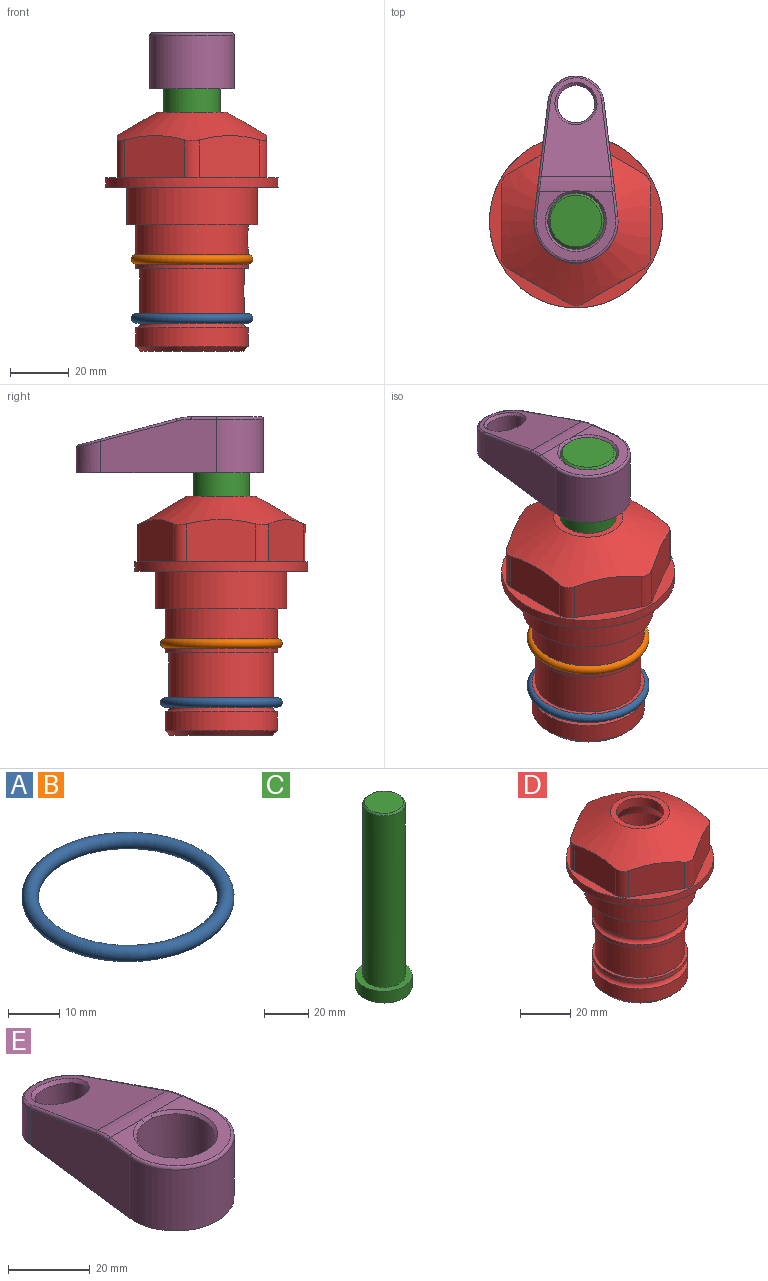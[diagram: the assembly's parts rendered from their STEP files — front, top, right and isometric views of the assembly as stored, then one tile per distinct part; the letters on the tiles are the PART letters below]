
ASSEMBLY  parts=5 mates=4
PART A: 1 faces, bbox 44.7x44.7x3.2 mm
  f0: torus R=19.05mm, axis (0,0,1), area 1193.9mm2
PART B: same geometry as A
PART C: 6 faces, bbox 25.4x25.4x101.6 mm
  f0: plane 17.46x17.46mm, normal (0,0,1), area 239.5mm2, adj f5
  f1: plane 25.4x25.4mm, normal (0,0,-1), area 506.7mm2, adj f2
  f2: cylinder r=12.7mm len=25.4mm, axis (0,0,1), area 506.7mm2, adj f1,f3
  f3: plane 25.4x25.4mm, normal (0,0,1), area 221.7mm2, adj f2,f4
  f4: cylinder r=9.53mm len=94.46mm, axis (0,0,1), area 5653mm2, adj f3,f5
  f5: cone r=8.73mm half-angle=45deg, axis (0,0,-1), area 64.4mm2, adj f0,f4
PART D: 36 faces, bbox 58.7x58.7x81 mm
  f0: cylinder r=17.78mm len=35.56mm, axis (0,0,1), area 1670.8mm2, adj f23,f24,f31
  f1: cylinder r=19.05mm len=38.1mm, axis (0,0,1), area 1191.9mm2, adj f26,f27,f30
  f2: plane 58.66x58.66mm, normal (0,0,-1), area 1150.6mm2, adj f3,f28
  f3: cylinder r=29.33mm len=58.66mm, axis (0,0,-1), area 585.1mm2, adj f2,f4
  f4: plane 58.66x58.66mm, normal (0,0,1), area 475.9mm2, adj f3,f5,f6,f7,f8,f9,f10,f11
  f5: plane 20.32x14.34mm, normal (-0.5,0.87,0), area 324.4mm2, adj f4,f15,f16,f17
  f6: plane 20.32x14.34mm, normal (0.5,0.87,0), area 324.4mm2, adj f4,f14,f15,f17
  f7: plane 23.48x14.34mm, normal (1,0,0), area 324.4mm2, adj f4,f13,f14,f17
  f8: plane 20.32x14.34mm, normal (0.5,-0.87,0), area 324.4mm2, adj f4,f12,f13,f17
  f9: plane 20.32x14.34mm, normal (-0.5,-0.87,0), area 324.4mm2, adj f4,f11,f12,f17
  f10: plane 23.48x14.34mm, normal (-1,0,0), area 324.4mm2, adj f4,f11,f16,f17
  f11: cylinder r=5.08mm len=12.85mm, axis (0,0,-1), area 67.2mm2, adj f4,f9,f10,f17
  f12: cylinder r=5.08mm len=12.85mm, axis (0,0,-1), area 67.2mm2, adj f4,f8,f9,f17
  f13: cylinder r=5.08mm len=12.85mm, axis (0,0,-1), area 67.2mm2, adj f4,f7,f8,f17
  f14: cylinder r=5.08mm len=12.85mm, axis (0,0,-1), area 67.2mm2, adj f4,f6,f7,f17
  f15: cylinder r=5.08mm len=12.85mm, axis (0,0,-1), area 67.2mm2, adj f4,f5,f6,f17
  f16: cylinder r=5.08mm len=12.85mm, axis (0,0,-1), area 67.2mm2, adj f4,f5,f10,f17
  f17: cone r=11.73mm half-angle=60deg, axis (0,0,-1), area 2071.8mm2, adj f5,f6,f7,f8,f9,f10,f11,f12
  f18: plane 23.46x23.46mm, normal (0,0,1), area 147.4mm2, adj f17,f35
  f19: plane 34.93x34.93mm, normal (0,0,-1), area 958mm2, adj f29
  f20: cylinder r=19.05mm len=38.1mm, axis (0,0,1), area 760.1mm2, adj f21,f29
  f21: torus R=19.05mm, axis (0,0,1), area 565.3mm2, adj f20,f22
  f22: cylinder r=19.05mm len=38.1mm, axis (0,0,1), area 190mm2, adj f21,f23
  f23: plane 38.1x38.1mm, normal (0,0,1), area 146.9mm2, adj f0,f22
  f24: plane 38.1x38.1mm, normal (0,0,-1), area 146.9mm2, adj f0,f25
  f25: cylinder r=19.05mm len=38.1mm, axis (0,0,1), area 190mm2, adj f24,f26
  f26: torus R=19.05mm, axis (0,0,1), area 565.3mm2, adj f1,f25
  f27: plane 44.45x44.45mm, normal (0,0,-1), area 411.7mm2, adj f1,f28
  f28: cylinder r=22.23mm len=44.45mm, axis (0,0,1), area 1773.5mm2, adj f2,f27
  f29: cone r=19.05mm half-angle=45deg, axis (0,0,1), area 257.5mm2, adj f19,f20
  f30: cylinder r=3.17mm len=6.75mm, axis (-1,0,0), area 128mm2, adj f1,f33
  f31: cylinder r=3.17mm len=6.35mm, axis (-1,0,0), area 102.5mm2, adj f0,f33
  f32: plane 25.4x25.4mm, normal (0,0,1), area 506.7mm2, adj f33
  f33: cylinder r=12.7mm len=66.42mm, axis (0,0,-1), area 5236.2mm2, adj f30,f31,f32,f34
  f34: cone r=9.53mm half-angle=30deg, axis (0,0,-1), area 443.4mm2, adj f33,f35
  f35: cylinder r=9.53mm len=19.05mm, axis (0,0,-1), area 240.9mm2, adj f18,f34
PART E: 31 faces, bbox 31.7x65.5x19.8 mm
  f0: plane 39.12x18.26mm, normal (0.99,0.12,0), area 612.2mm2, adj f1,f4,f7,f11,f13,f15
  f1: cylinder r=9.53mm len=18.91mm, axis (0,0,-1), area 296.1mm2, adj f0,f2,f7,f17
  f2: plane 39.12x18.26mm, normal (-0.99,0.12,0), area 612.2mm2, adj f1,f4,f7,f12,f14,f16
  f3: cylinder r=6.35mm len=12.7mm, axis (0,0,-1), area 362.4mm2, adj f7,f18
  f4: cylinder r=14.29mm len=28.58mm, axis (0,0,-1), area 882.2mm2, adj f0,f2,f7,f10
  f5: cylinder r=9.53mm len=19.05mm, axis (0,0,-1), area 1092.6mm2, adj f7,f19,f20
  f6: plane 26.99x23.69mm, normal (0,0,1), area 216.2mm2, adj f9,f10,f11,f12,f19
  f7: plane 63.5x28.58mm, normal (0,0,-1), area 661.8mm2, adj f0,f1,f2,f3,f4,f5,f22,f23
  f8: plane 33.52x23.6mm, normal (0,0.26,0.97), area 486mm2, adj f9,f15,f16,f17,f18
  f9: cylinder r=19.05mm len=24.72mm, axis (1,0,0), area 120.4mm2, adj f6,f8,f13,f14,f20
  f10: torus R=13.49mm, axis (0,0,1), area 59mm2, adj f4,f6,f11,f12
  f11: cylinder r=0.79mm len=8.67mm, axis (0.12,-0.99,0), area 10.8mm2, adj f0,f6,f10,f13
  f12: cylinder r=0.79mm len=8.67mm, axis (0.12,0.99,0), area 10.8mm2, adj f2,f6,f10,f14
  f13: bspline ~4.95x1.42mm, area 6.1mm2, adj f0,f9,f11,f15
  f14: bspline ~4.95x1.42mm, area 6.1mm2, adj f2,f9,f12,f16
  f15: cylinder r=0.79mm len=25.95mm, axis (0.12,-0.96,0.26), area 32.9mm2, adj f0,f8,f13,f17
  f16: cylinder r=0.79mm len=25.95mm, axis (0.12,0.96,-0.26), area 32.9mm2, adj f2,f8,f14,f17
  f17: bspline ~18.91x8.38mm, area 30mm2, adj f1,f8,f15,f16
  f18: bspline ~14.29x14.29mm, area 48.3mm2, adj f3,f8
  f19: cone r=9.53mm half-angle=45deg, axis (0,0,1), area 66.5mm2, adj f5,f6,f20
  f20: bspline ~3.22x0.96mm, area 3.5mm2, adj f5,f9,f19
  f21: plane 2.75x2.72mm, normal (0,0,-1), area 2.9mm2, adj f23,f25,f28
  f22: plane 23.05x15.88mm, normal (-0.99,-0.12,0), area 323.6mm2, adj f7,f25,f26,f27,f28,f29
  f23: plane 23.05x15.88mm, normal (0.99,-0.12,0), area 323.6mm2, adj f7,f21,f25,f27,f28,f30
  f24: cylinder r=9.53mm len=10.69mm, axis (0,0,-1), area 114.7mm2, adj f7,f27,f29,f30
  f25: cylinder r=12.7mm len=20.59mm, axis (0,0,-1), area 381.1mm2, adj f7,f21,f22,f23,f26,f28
  f26: plane 2.75x2.72mm, normal (0,0,-1), area 2.9mm2, adj f22,f25,f28
  f27: plane 19.72x18.37mm, normal (0,-0.26,-0.97), area 291.8mm2, adj f22,f23,f24,f28,f29,f30
  f28: cylinder r=15.88mm len=19.92mm, axis (1,0,0), area 54.8mm2, adj f21,f22,f23,f25,f26,f27
  f29: cylinder r=1.59mm len=11mm, axis (0,0,-1), area 34.7mm2, adj f7,f22,f24,f27
  f30: cylinder r=1.59mm len=11mm, axis (0,0,-1), area 34.7mm2, adj f7,f23,f24,f27
PLACE A t=(0,0,-20)mm
PLACE B at identity
PLACE C t=(0,0,-11.18)mm
PLACE D at identity fixed
PLACE E t=(0,0,-11.18)mm
MATE fastened E.f4 <-> C.f2  axis (0,0,1) through (0,0,52.32)mm
MATE fastened C.f2 <-> D.f0  axis (0,0,1) through (0,0,52.32)mm
MATE fastened D.f0 <-> A.f0  axis (0,0,1) through (0,0,-44.51)mm
MATE cylindrical C.f2 <-> D.f0  axis (0,0,1) through (0,0,-42.93)mm
